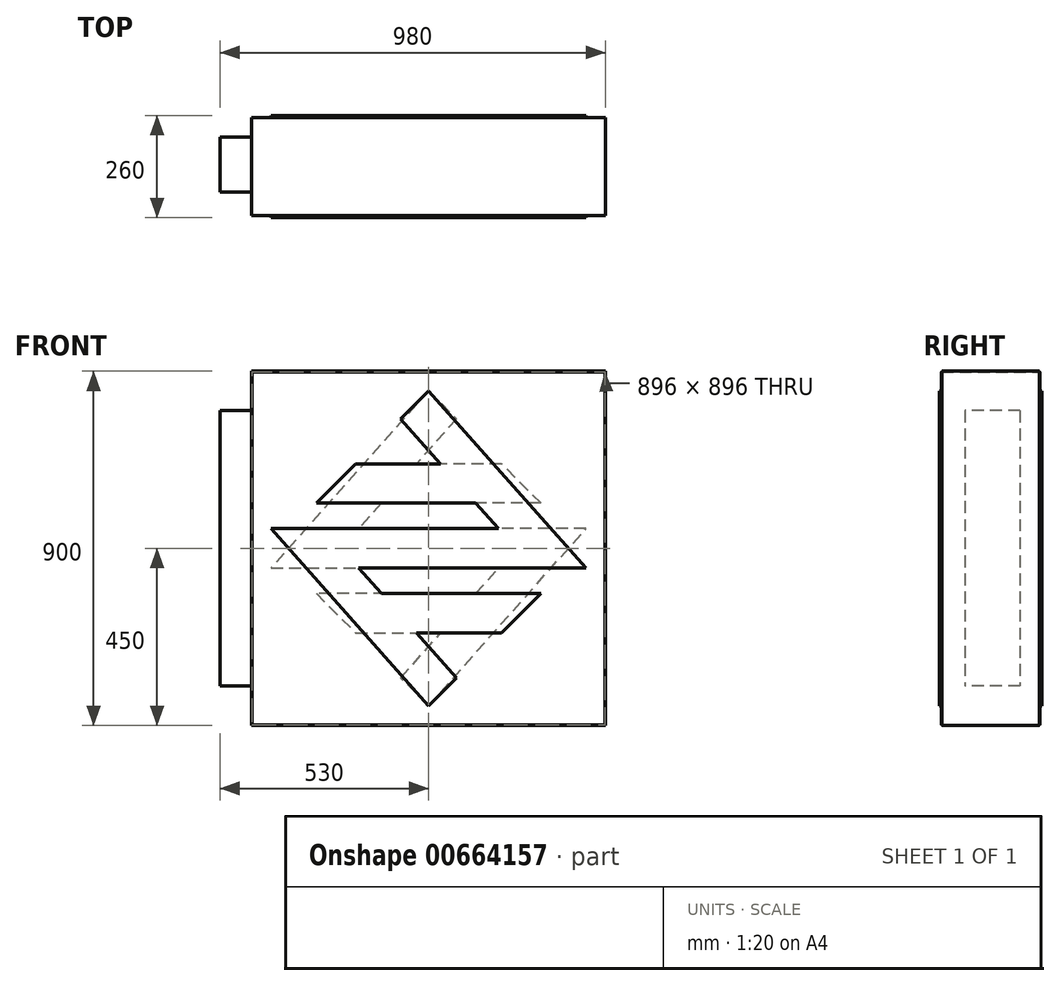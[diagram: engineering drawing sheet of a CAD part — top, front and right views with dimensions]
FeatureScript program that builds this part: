
annotation { "Feature Type Name" : "Feature", "Feature Type Description" : "" }
export const myFeature = defineFeature(function(context is Context, id is Id, definition is map)
    precondition{}
    {
        {
            var Q0;
            Q0=qCreatedBy(makeId("Front.planeOp"),FACE);
            var sketch = newSketch(context, id + "F0", { "sketchPlane" : qUnion([Q0])});
            skLineSegment(sketch, "E0.bottom", {"start": v(-450, 450) * mm, "end": v(450, 450) * mm});
            skLineSegment(sketch, "E0.top", {"start": v(-450, -450) * mm, "end": v(450, -450) * mm});
            skLineSegment(sketch, "E0.left", {"start": v(-450, 450) * mm, "end": v(-450, -450) * mm, "construction": true});
            skLineSegment(sketch, "E0.right", {"start": v(450, 450) * mm, "end": v(450, -450) * mm});
            skPoint(sketch, "E1.firstSnap0", {"position": v(0, -450) * mm});
            skPoint(sketch, "E1.oppositeSnap0", {"position": v(0, -450) * mm});
            skLineSegment(sketch, "E2", {"start": v(-450, 450) * mm, "end": v(-450, 450) * mm});
            skLineSegment(sketch, "E3", {"start": v(-450, 450) * mm, "end": v(-450, -450) * mm});
            skLineSegment(sketch, "E4", {"start": v(-450, -450) * mm, "end": v(-450, -450) * mm});
            skSolve(sketch);
        }
        {
            var Q0;
            Q0=makeQuery(id+"F0.imprint","IMPRINT",FACE,{"disambiguationData":[TD([[makeQuery(id+"F0.imprint","IMPRINT",EDGE,{"derivedFrom":sQuery(id+"F0.wireOp",EDGE,"E0.bottom")}),-1.0]])]});
            extrude(context, id + "F1", {"entities" : qUnion([Q0]), "depth" : 250 * mm, "offsetDistance" : 25 * mm, "symmetric" : true});
        }
        {
            var Q0;
            Q0=makeQuery(id+"F1.opExtrude","CAP_FACE",FACE,{"disambiguationData":[OSD([sQuery(id+"F0.wireOp",EDGE,"E0.bottom"),sQuery(id+"F0.wireOp",EDGE,"E0.top"),sQuery(id+"F0.wireOp",EDGE,"E0.right"),sQuery(id+"F0.wireOp",EDGE,"E2"),sQuery(id+"F0.wireOp",EDGE,"E3"),sQuery(id+"F0.wireOp",EDGE,"E4")])],"isStart":false});
            var sketch = newSketch(context, id + "F2", { "sketchPlane" : qUnion([Q0])});
            skLineSegment(sketch, "E5.bottom", {"start": v(-400, 400) * mm, "end": v(400, 400) * mm, "construction": true});
            skLineSegment(sketch, "E5.top", {"start": v(-400, -400) * mm, "end": v(400, -400) * mm, "construction": true});
            skLineSegment(sketch, "E5.left", {"start": v(-400, 400) * mm, "end": v(-400, -400) * mm, "construction": true});
            skLineSegment(sketch, "E5.right", {"start": v(400, 400) * mm, "end": v(400, -400) * mm, "construction": true});
            skLineSegment(sketch, "E6", {"start": v(0, 400) * mm, "end": v(0, -400) * mm, "construction": true});
            skLineSegment(sketch, "E7", {"start": v(-400, 0) * mm, "end": v(400, 0) * mm, "construction": true});
            skLineSegment(sketch, "E8", {"start": v(0, -400) * mm, "end": v(-400, 50) * mm});
            skLineSegment(sketch, "E9", {"start": v(0, 400) * mm, "end": v(400, -50) * mm});
            skLineSegment(sketch, "E10", {"start": v(-400, 0) * mm, "end": v(0, 400) * mm, "construction": true});
            skLineSegment(sketch, "E11", {"start": v(0, 400) * mm, "end": v(-70.71, 329.29) * mm});
            skLineSegment(sketch, "E12", {"start": v(-400, 50) * mm, "end": v(177.55, 50) * mm});
            skLineSegment(sketch, "E13", {"start": v(-70.71, 329.29) * mm, "end": v(30.88, 215) * mm});
            skLineSegment(sketch, "E14", {"start": v(400, -50) * mm, "end": v(-177.55, -50) * mm});
            skLineSegment(sketch, "E15", {"start": v(0, -400) * mm, "end": v(400, 0) * mm, "construction": true});
            skLineSegment(sketch, "E16", {"start": v(0, -400) * mm, "end": v(70.71, -329.29) * mm});
            skLineSegment(sketch, "E17", {"start": v(70.71, -329.29) * mm, "end": v(-30.88, -215) * mm});
            skLineSegment(sketch, "E18", {"start": v(-119.77, -115) * mm, "end": v(285, -115) * mm});
            skLineSegment(sketch, "E19", {"start": v(285, -115) * mm, "end": v(185, -215) * mm});
            skLineSegment(sketch, "E20", {"start": v(185, -215) * mm, "end": v(-30.88, -215) * mm});
            skLineSegment(sketch, "E21.trimOffspring", {"start": v(-119.77, -115) * mm, "end": v(-177.55, -50) * mm});
            skLineSegment(sketch, "E22", {"start": v(-285, 115) * mm, "end": v(119.77, 115) * mm});
            skLineSegment(sketch, "E23", {"start": v(-285, 115) * mm, "end": v(-185, 215) * mm});
            skLineSegment(sketch, "E24", {"start": v(-185, 215) * mm, "end": v(30.88, 215) * mm});
            skLineSegment(sketch, "E25.trimOffspring", {"start": v(119.77, 115) * mm, "end": v(177.55, 50) * mm});
            skSolve(sketch);
        }
        {
            var Q0;
            Q0=qSketchRegion(id+"F2",true);
            extrude(context, id + "F3", {"entities" : qUnion([Q0]), "depth" : 5 * mm, "offsetDistance" : 25 * mm});
        }
        {
            var Q0;
            Q0=makeQuery(id+"F3.opExtrude","SWEPT_BODY",BODY,{"disambiguationData":[OSD([sQuery(id+"F2.wireOp",EDGE,"E8"),sQuery(id+"F2.wireOp",EDGE,"E9"),sQuery(id+"F2.wireOp",EDGE,"E11"),sQuery(id+"F2.wireOp",EDGE,"E12"),sQuery(id+"F2.wireOp",EDGE,"E13"),sQuery(id+"F2.wireOp",EDGE,"E14"),sQuery(id+"F2.wireOp",EDGE,"E16"),sQuery(id+"F2.wireOp",EDGE,"E17"),sQuery(id+"F2.wireOp",EDGE,"E18"),sQuery(id+"F2.wireOp",EDGE,"E19"),sQuery(id+"F2.wireOp",EDGE,"E20"),sQuery(id+"F2.wireOp",EDGE,"E21.trimOffspring"),sQuery(id+"F2.wireOp",EDGE,"E22"),sQuery(id+"F2.wireOp",EDGE,"E23"),sQuery(id+"F2.wireOp",EDGE,"E24"),sQuery(id+"F2.wireOp",EDGE,"E25.trimOffspring")])]});
            var Q1;
            Q1=qCreatedBy(makeId("Front.planeOp"),FACE);
            mirror(context, id + "F4", {"entities" : qUnion([Q0]), "mirrorPlane" : qUnion([Q1])});
        }
        {
            var Q0;
            Q0=makeQuery(id+"F4.opPattern","COPY",BODY,{"derivedFrom":makeQuery(id+"F3.opExtrude","SWEPT_BODY",BODY,{"disambiguationData":[OSD([sQuery(id+"F2.wireOp",EDGE,"E8"),sQuery(id+"F2.wireOp",EDGE,"E9"),sQuery(id+"F2.wireOp",EDGE,"E11"),sQuery(id+"F2.wireOp",EDGE,"E12"),sQuery(id+"F2.wireOp",EDGE,"E13"),sQuery(id+"F2.wireOp",EDGE,"E14"),sQuery(id+"F2.wireOp",EDGE,"E16"),sQuery(id+"F2.wireOp",EDGE,"E17"),sQuery(id+"F2.wireOp",EDGE,"E18"),sQuery(id+"F2.wireOp",EDGE,"E19"),sQuery(id+"F2.wireOp",EDGE,"E20"),sQuery(id+"F2.wireOp",EDGE,"E21.trimOffspring"),sQuery(id+"F2.wireOp",EDGE,"E22"),sQuery(id+"F2.wireOp",EDGE,"E23"),sQuery(id+"F2.wireOp",EDGE,"E24"),sQuery(id+"F2.wireOp",EDGE,"E25.trimOffspring")])]}),"instanceName":"1"});
            var Q1;
            Q1=qCreatedBy(makeId("Right.planeOp"),FACE);
            mirror(context, id + "F5", {"entities" : qUnion([Q0]), "mirrorPlane" : qUnion([Q1])});
        }
        {
            var Q0;
            Q0=makeQuery(id+"F1.opExtrude","CAP_FACE",FACE,{"disambiguationData":[OSD([sQuery(id+"F0.wireOp",EDGE,"E0.bottom"),sQuery(id+"F0.wireOp",EDGE,"E0.top"),sQuery(id+"F0.wireOp",EDGE,"E0.right"),sQuery(id+"F0.wireOp",EDGE,"E3")])],"isStart":false});
            var sketch = newSketch(context, id + "F6", { "sketchPlane" : qUnion([Q0])});
            skLineSegment(sketch, "E26.0", {"start": v(-450, 450) * mm, "end": v(450, 450) * mm});
            skLineSegment(sketch, "E26.1", {"start": v(-450, 450) * mm, "end": v(-450, -450) * mm});
            skLineSegment(sketch, "E26.2", {"start": v(450, 450) * mm, "end": v(450, -450) * mm});
            skLineSegment(sketch, "E26.3", {"start": v(-450, -450) * mm, "end": v(450, -450) * mm});
            skLineSegment(sketch, "E27.0", {"start": v(-448, -448) * mm, "end": v(448, -448) * mm});
            skLineSegment(sketch, "E27.1", {"start": v(-448, 448) * mm, "end": v(-448, -448) * mm});
            skLineSegment(sketch, "E27.2", {"start": v(-448, 448) * mm, "end": v(448, 448) * mm});
            skLineSegment(sketch, "E27.3", {"start": v(448, 448) * mm, "end": v(448, -448) * mm});
            skSolve(sketch);
        }
        {
            var Q0;
            Q0 = qSketchRegion(id + "F6", true);
            extrude(context, id + "F7", {"entities" : qUnion([Q0]), "operationType" : NewBodyOperationType.REMOVE, "endBound" : BoundingType.THROUGH_ALL, "oppositeDirection" : true, "depth" : 25 * mm, "offsetDistance" : 25 * mm});
        }
        {
            var Q0;
            Q0=makeQuery(id+"F1.opExtrude","CAP_FACE",FACE,{"disambiguationData":[OSD([sQuery(id+"F0.wireOp",EDGE,"E0.bottom"),sQuery(id+"F0.wireOp",EDGE,"E0.top"),sQuery(id+"F0.wireOp",EDGE,"E0.right"),sQuery(id+"F0.wireOp",EDGE,"E3")])],"isStart":true});
            cPlane(context, id + "F8", {"entities" : qUnion([Q0]), "cplaneType" : CPlaneType.OFFSET, "offset" : 1 * mm, "oppositeDirection" : true, "width" : 150 * mm, "height" : 150 * mm});
        }
        {
            var Q0;
            Q0=qCreatedBy(id+"F8.planeOp",FACE);
            var sketch = newSketch(context, id + "F9", { "sketchPlane" : qUnion([Q0])});
            skLineSegment(sketch, "E28.0", {"start": v(450, 450) * mm, "end": v(-450, 450) * mm});
            skLineSegment(sketch, "E28.1", {"start": v(450, 450) * mm, "end": v(450, -450) * mm});
            skLineSegment(sketch, "E28.2", {"start": v(-450, 450) * mm, "end": v(-450, -450) * mm});
            skLineSegment(sketch, "E28.3", {"start": v(450, -450) * mm, "end": v(-450, -450) * mm});
            skLineSegment(sketch, "E28.4", {"start": v(448, -448) * mm, "end": v(-448, -448) * mm});
            skLineSegment(sketch, "E28.5", {"start": v(448, 448) * mm, "end": v(448, -448) * mm});
            skLineSegment(sketch, "E28.6", {"start": v(448, 448) * mm, "end": v(-448, 448) * mm});
            skLineSegment(sketch, "E28.7", {"start": v(-448, 448) * mm, "end": v(-448, -448) * mm});
            skSolve(sketch);
        }
        {
            var Q0;
            Q0 = qSketchRegion(id + "F9", true);
            extrude(context, id + "F10", {"entities" : qUnion([Q0]), "oppositeDirection" : true, "depth" : 248 * mm, "offsetDistance" : 25 * mm});
        }
        {
            var Q0;
            Q0=makeQuery(id+"F10.opExtrude","SWEPT_FACE",FACE,{"disambiguationData":[OSD([sQuery(id+"F9.wireOp",EDGE,"E28.1")])]});
            var sketch = newSketch(context, id + "F11", { "sketchPlane" : qUnion([Q0])});
            skLineSegment(sketch, "E29", {"start": v(0, 450) * mm, "end": v(0, -450) * mm, "construction": true});
            skLineSegment(sketch, "E30", {"start": v(-124, 0) * mm, "end": v(124, 0) * mm, "construction": true});
            skLineSegment(sketch, "E31.bottom", {"start": v(-75, 350) * mm, "end": v(65, 350) * mm});
            skLineSegment(sketch, "E31.top", {"start": v(-75, -350) * mm, "end": v(65, -350) * mm});
            skLineSegment(sketch, "E31.left", {"start": v(-75, 350) * mm, "end": v(-75, -350) * mm});
            skLineSegment(sketch, "E31.right", {"start": v(65, 350) * mm, "end": v(65, -350) * mm});
            skSolve(sketch);
        }
        {
            var Q0;
            Q0 = qSketchRegion(id + "F11", true);
            extrude(context, id + "F12", {"entities" : qUnion([Q0]), "depth" : 80 * mm, "offsetDistance" : 25 * mm});
        }
    });
